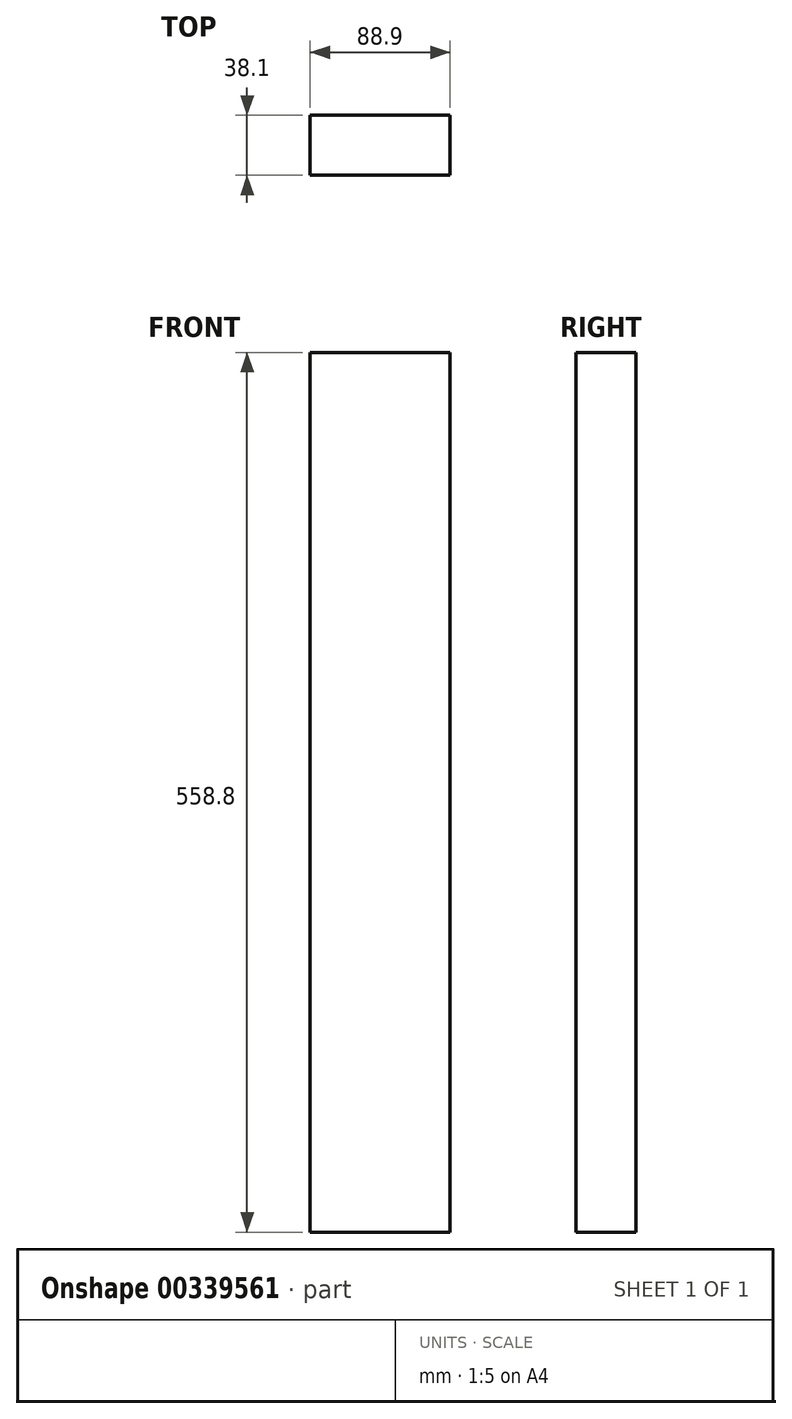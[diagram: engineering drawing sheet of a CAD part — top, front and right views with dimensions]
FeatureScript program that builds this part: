
annotation { "Feature Type Name" : "Feature", "Feature Type Description" : "" }
export const myFeature = defineFeature(function(context is Context, id is Id, definition is map)
    precondition{}
    {
        {
            var Q0;
            Q0=qCreatedBy(makeId("Top.planeOp"),FACE);
            var sketch = newSketch(context, id + "F0", { "sketchPlane" : qUnion([Q0])});
            skLineSegment(sketch, "E0.bottom", {"start": v(44.45, 19.05) * mm, "end": v(-44.45, 19.05) * mm});
            skLineSegment(sketch, "E0.top", {"start": v(44.45, -19.05) * mm, "end": v(-44.45, -19.05) * mm});
            skLineSegment(sketch, "E0.left", {"start": v(44.45, 19.05) * mm, "end": v(44.45, -19.05) * mm});
            skLineSegment(sketch, "E0.right", {"start": v(-44.45, 19.05) * mm, "end": v(-44.45, -19.05) * mm});
            skPoint(sketch, "E0.middle", {"position": v(0, 0) * mm});
            skSolve(sketch);
        }
        {
            var Q0;
            Q0 = qSketchRegion(id + "F0", true);
            extrude(context, id + "F1", {"entities" : qUnion([Q0]), "depth" : 558.8 * mm});
        }
    });
